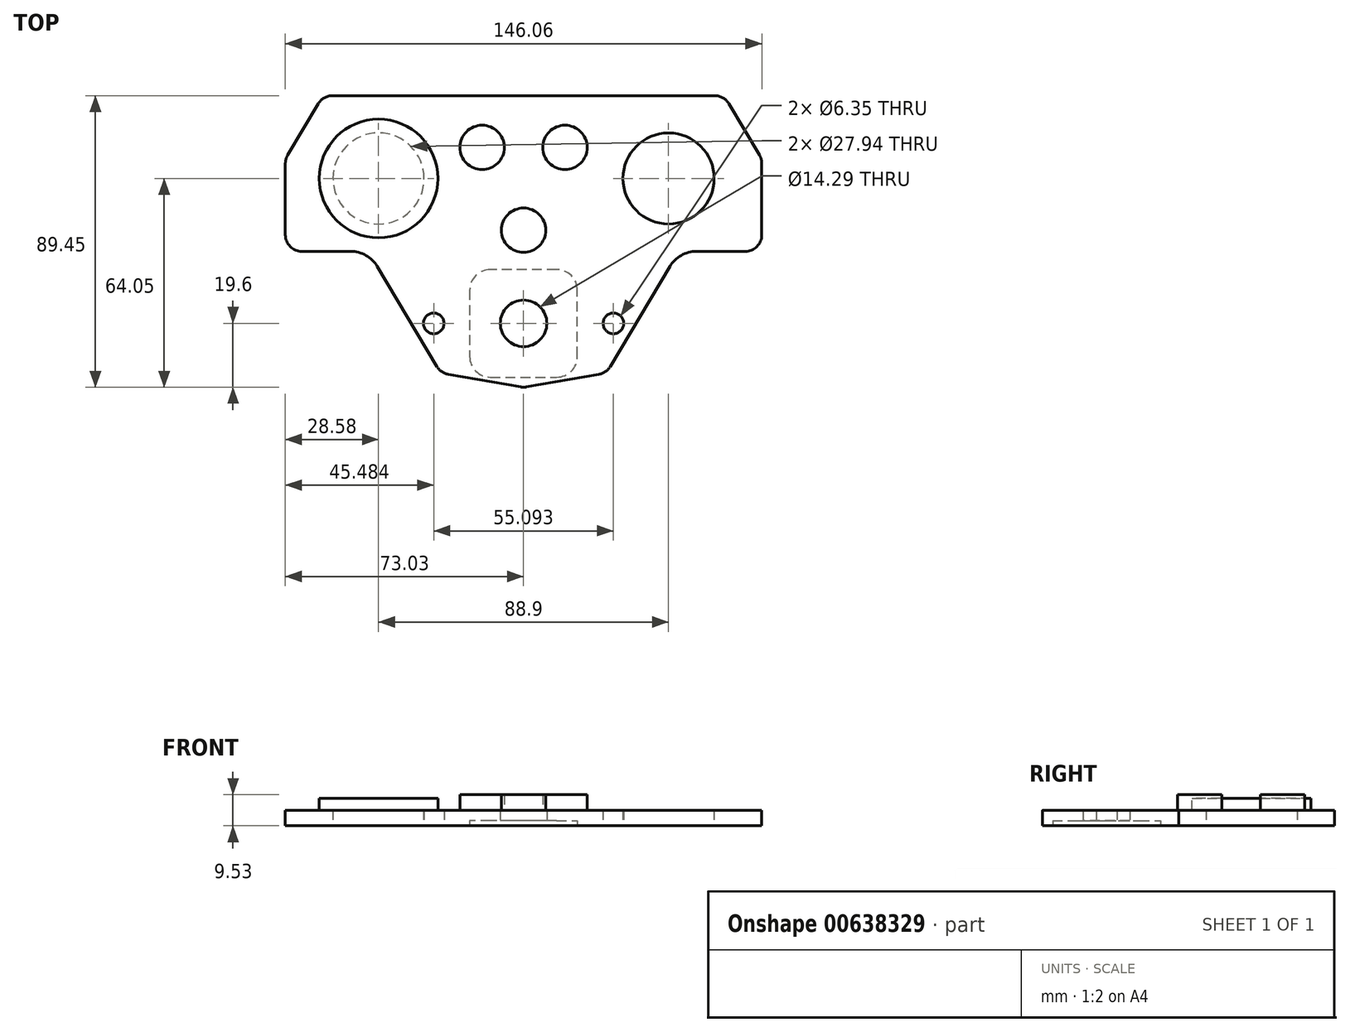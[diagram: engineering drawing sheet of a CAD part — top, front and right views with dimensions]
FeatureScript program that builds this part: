
annotation { "Feature Type Name" : "Feature", "Feature Type Description" : "" }
export const myFeature = defineFeature(function(context is Context, id is Id, definition is map)
    precondition{}
    {
        {
            var Q0;
            Q0=qCreatedBy(makeId("Top.planeOp"),FACE);
            var sketch = newSketch(context, id + "F0", { "sketchPlane" : qUnion([Q0])});
            skCircle(sketch, "E0", {"center": v(0, 0) * mm, "radius": 7.14 * mm});
            skCircle(sketch, "E1", {"center": v(27.55, 0) * mm, "radius": 3.18 * mm});
            skCircle(sketch, "E2", {"center": v(-27.55, 0) * mm, "radius": 3.18 * mm});
            skLineSegment(sketch, "E3", {"start": v(0, 29.39) * mm, "end": v(0, -33.87) * mm, "construction": true});
            skLineSegment(sketch, "E4", {"start": v(-25.4, -15.2) * mm, "end": v(0, -19.68) * mm});
            skLineSegment(sketch, "E5", {"start": v(0, -19.68) * mm, "end": v(25.4, -15.2) * mm});
            skLineSegment(sketch, "E6", {"start": v(-25.4, -15.2) * mm, "end": v(-47.63, 22.1) * mm});
            skLineSegment(sketch, "E7", {"start": v(25.4, -15.2) * mm, "end": v(47.63, 22.1) * mm});
            skLineSegment(sketch, "E8", {"start": v(47.63, 22.1) * mm, "end": v(73.03, 22.1) * mm});
            skLineSegment(sketch, "E9", {"start": v(73.03, 22.1) * mm, "end": v(73.03, 50.43) * mm});
            skLineSegment(sketch, "E10", {"start": v(73.03, 50.43) * mm, "end": v(61.45, 69.85) * mm});
            skLineSegment(sketch, "E11", {"start": v(61.45, 69.85) * mm, "end": v(0, 69.85) * mm});
            skLineSegment(sketch, "E12.MirrorCS", {"start": v(-61.45, 69.85) * mm, "end": v(0, 69.85) * mm});
            skLineSegment(sketch, "E13.MirrorCS", {"start": v(-73.03, 50.43) * mm, "end": v(-61.45, 69.85) * mm});
            skLineSegment(sketch, "E14.MirrorCS", {"start": v(-73.03, 22.1) * mm, "end": v(-73.03, 50.43) * mm});
            skLineSegment(sketch, "E15.MirrorCS", {"start": v(-47.63, 22.1) * mm, "end": v(-73.03, 22.1) * mm});
            skCircle(sketch, "E16", {"center": v(-51.23, 15.75) * mm, "radius": 6.35 * mm, "construction": true});
            skCircle(sketch, "E17", {"center": v(51.23, 15.75) * mm, "radius": 6.35 * mm, "construction": true});
            skSolve(sketch);
        }
        {
            var Q0;
            Q0=makeQuery(id+"F0.imprint","IMPRINT",FACE,{"disambiguationData":[TD([[makeQuery(id+"F0.imprint","IMPRINT",EDGE,{"derivedFrom":sQuery(id+"F0.wireOp",EDGE,"E0")}),-1.0]])]});
            extrude(context, id + "F1", {"entities" : qUnion([Q0]), "depth" : 4.76 * mm, "offsetDistance" : 25.4 * mm});
        }
        {
            var Q0;
            Q0=makeQuery(id+"F1.opExtrude","SWEPT_EDGE",EDGE,{"disambiguationData":[OSD([sQuery(id+"F0.wireOp",EDGE,"E6"),sQuery(id+"F0.wireOp",EDGE,"E15.MirrorCS")])]});
            var Q1;
            Q1=makeQuery(id+"F1.opExtrude","SWEPT_EDGE",EDGE,{"disambiguationData":[OSD([sQuery(id+"F0.wireOp",EDGE,"E7"),sQuery(id+"F0.wireOp",EDGE,"E8")])]});
            fillet(context, id + "F2", {"entities" : qUnion([Q0, Q1]), "radius" : 9.52 * mm, "tangentPropagation" : true, "allowEdgeOverflow" : false});
        }
        {
            var Q0;
            Q0=makeQuery(id+"F1.opExtrude","SWEPT_EDGE",EDGE,{"disambiguationData":[OSD([sQuery(id+"F0.wireOp",EDGE,"E14.MirrorCS"),sQuery(id+"F0.wireOp",EDGE,"E15.MirrorCS")])]});
            var Q1;
            Q1=makeQuery(id+"F1.opExtrude","SWEPT_EDGE",EDGE,{"disambiguationData":[OSD([sQuery(id+"F0.wireOp",EDGE,"E4"),sQuery(id+"F0.wireOp",EDGE,"E6")])]});
            var Q2;
            Q2=makeQuery(id+"F1.opExtrude","SWEPT_EDGE",EDGE,{"disambiguationData":[OSD([sQuery(id+"F0.wireOp",EDGE,"E4"),sQuery(id+"F0.wireOp",EDGE,"E5")])]});
            var Q3;
            Q3=makeQuery(id+"F1.opExtrude","SWEPT_EDGE",EDGE,{"disambiguationData":[OSD([sQuery(id+"F0.wireOp",EDGE,"E5"),sQuery(id+"F0.wireOp",EDGE,"E7")])]});
            var Q4;
            Q4=makeQuery(id+"F1.opExtrude","SWEPT_EDGE",EDGE,{"disambiguationData":[OSD([sQuery(id+"F0.wireOp",EDGE,"E8"),sQuery(id+"F0.wireOp",EDGE,"E9")])]});
            var Q5;
            Q5=makeQuery(id+"F1.opExtrude","SWEPT_EDGE",EDGE,{"disambiguationData":[OSD([sQuery(id+"F0.wireOp",EDGE,"E9"),sQuery(id+"F0.wireOp",EDGE,"E10")])]});
            var Q6;
            Q6=makeQuery(id+"F1.opExtrude","SWEPT_EDGE",EDGE,{"disambiguationData":[OSD([sQuery(id+"F0.wireOp",EDGE,"E10"),sQuery(id+"F0.wireOp",EDGE,"E11")])]});
            var Q7;
            Q7=makeQuery(id+"F1.opExtrude","SWEPT_EDGE",EDGE,{"disambiguationData":[OSD([sQuery(id+"F0.wireOp",EDGE,"E13.MirrorCS"),sQuery(id+"F0.wireOp",EDGE,"E14.MirrorCS")])]});
            var Q8;
            Q8=makeQuery(id+"F1.opExtrude","SWEPT_EDGE",EDGE,{"disambiguationData":[OSD([sQuery(id+"F0.wireOp",EDGE,"E12.MirrorCS"),sQuery(id+"F0.wireOp",EDGE,"E13.MirrorCS")])]});
            fillet(context, id + "F3", {"entities" : qUnion([Q0, Q1, Q2, Q3, Q4, Q5, Q6, Q7, Q8]), "radius" : 5.08 * mm, "tangentPropagation" : true, "allowEdgeOverflow" : false});
        }
        {
            var Q0;
            Q0=qCreatedBy(makeId("Top.planeOp"),FACE);
            var sketch = newSketch(context, id + "F4", { "sketchPlane" : qUnion([Q0])});
            skCircle(sketch, "E18", {"center": v(-44.45, 44.45) * mm, "radius": 13.97 * mm});
            skLineSegment(sketch, "E19", {"start": v(0, 0) * mm, "end": v(0, 69.85) * mm, "construction": true});
            skCircle(sketch, "E20.MirrorC", {"center": v(44.45, 44.45) * mm, "radius": 13.97 * mm});
            skSolve(sketch);
        }
        {
            var Q0;
            Q0 = qSketchRegion(id + "F4", true);
            extrude(context, id + "F5", {"entities" : qUnion([Q0]), "operationType" : NewBodyOperationType.REMOVE, "depth" : 25.4 * mm, "offsetDistance" : 25.4 * mm});
        }
        {
            var Q0;
            Q0=qCreatedBy(makeId("Top.planeOp"),FACE);
            var sketch = newSketch(context, id + "F6", { "sketchPlane" : qUnion([Q0])});
            skArc(sketch, "E21", {"start": v(-16.51, -10.16) * mm, "mid": v(-14.65, -14.65) * mm, "end": v(-10.16, -16.51) * mm});
            skArc(sketch, "E22", {"start": v(-10.16, 16.51) * mm, "mid": v(-14.65, 14.65) * mm, "end": v(-16.51, 10.16) * mm});
            skLineSegment(sketch, "E23", {"start": v(-23.42, 0) * mm, "end": v(23.42, 0) * mm, "construction": true});
            skLineSegment(sketch, "E24", {"start": v(0, -20.58) * mm, "end": v(0, 20.58) * mm, "construction": true});
            skArc(sketch, "E25.MirrorC", {"start": v(10.16, 16.51) * mm, "mid": v(14.65, 14.65) * mm, "end": v(16.51, 10.16) * mm});
            skArc(sketch, "E26.MirrorC", {"start": v(16.51, -10.16) * mm, "mid": v(14.65, -14.65) * mm, "end": v(10.16, -16.51) * mm});
            skLineSegment(sketch, "E27", {"start": v(-10.16, -16.51) * mm, "end": v(10.16, -16.51) * mm});
            skLineSegment(sketch, "E28", {"start": v(16.51, -10.16) * mm, "end": v(16.51, 10.16) * mm});
            skLineSegment(sketch, "E29", {"start": v(10.16, 16.51) * mm, "end": v(-10.16, 16.51) * mm});
            skLineSegment(sketch, "E30", {"start": v(-16.51, 10.16) * mm, "end": v(-16.51, -10.16) * mm});
            skSolve(sketch);
        }
        {
            var Q0;
            Q0=makeQuery(id+"F6.imprint","IMPRINT",FACE,{"disambiguationData":[TD([[makeQuery(id+"F6.imprint","IMPRINT",EDGE,{"derivedFrom":sQuery(id+"F6.wireOp",EDGE,"E21")}),1.0]])]});
            extrude(context, id + "F7", {"entities" : qUnion([Q0]), "operationType" : NewBodyOperationType.REMOVE, "depth" : 1.52 * mm, "offsetDistance" : 25.4 * mm});
        }
        {
            var Q0;
            Q0=qCreatedBy(makeId("Front.planeOp"),FACE);
            cPlane(context, id + "F8", {"entities" : qUnion([Q0]), "cplaneType" : CPlaneType.OFFSET, "offset" : 44.45 * mm, "oppositeDirection" : true, "width" : 152.4 * mm, "height" : 152.4 * mm});
        }
        {
            var Q0;
            Q0=qCreatedBy(makeId("Right.planeOp"),FACE);
            cPlane(context, id + "F9", {"entities" : qUnion([Q0]), "cplaneType" : CPlaneType.OFFSET, "offset" : 44.45 * mm, "oppositeDirection" : true, "width" : 152.4 * mm, "height" : 152.4 * mm});
        }
        {
            var Q0;
            Q0=qCreatedBy(id+"F8.planeOp",FACE);
            var sketch = newSketch(context, id + "F10", { "sketchPlane" : qUnion([Q0])});
            skLineSegment(sketch, "E31", {"start": v(-44.45, 30.16) * mm, "end": v(-44.45, -35.09) * mm, "construction": true});
            skLineSegment(sketch, "E32.bottom", {"start": v(-44.45, 8.4) * mm, "end": v(-26.26, 8.4) * mm});
            skLineSegment(sketch, "E32.top", {"start": v(-44.45, 4.76) * mm, "end": v(-26.26, 4.76) * mm});
            skLineSegment(sketch, "E32.left", {"start": v(-44.45, 8.4) * mm, "end": v(-44.45, 4.76) * mm});
            skLineSegment(sketch, "E32.right", {"start": v(-26.26, 8.4) * mm, "end": v(-26.26, 4.76) * mm});
            skSolve(sketch);
        }
        {
            var Q0;
            Q0 = qSketchRegion(id + "F10", true);
            var Q1;
            Q1=sQuery(id+"F10.wireOp",EDGE,"E31");
            revolve(context, id + "F11", {"entities" : qUnion([Q0]), "axis" : qUnion([Q1]), "revolveType" : RevolveType.FULL});
        }
        {
            var Q0;
            Q0=makeQuery(id+"F1.opExtrude","CAP_FACE",FACE,{"disambiguationData":[OSD([sQuery(id+"F0.wireOp",EDGE,"E0"),sQuery(id+"F0.wireOp",EDGE,"E1"),sQuery(id+"F0.wireOp",EDGE,"E2"),sQuery(id+"F0.wireOp",EDGE,"E4"),sQuery(id+"F0.wireOp",EDGE,"E5"),sQuery(id+"F0.wireOp",EDGE,"E6"),sQuery(id+"F0.wireOp",EDGE,"E7"),sQuery(id+"F0.wireOp",EDGE,"E8"),sQuery(id+"F0.wireOp",EDGE,"E9"),sQuery(id+"F0.wireOp",EDGE,"E10"),sQuery(id+"F0.wireOp",EDGE,"E11"),sQuery(id+"F0.wireOp",EDGE,"E12.MirrorCS"),sQuery(id+"F0.wireOp",EDGE,"E13.MirrorCS"),sQuery(id+"F0.wireOp",EDGE,"E14.MirrorCS"),sQuery(id+"F0.wireOp",EDGE,"E15.MirrorCS")])],"isStart":false});
            var sketch = newSketch(context, id + "F12", { "sketchPlane" : qUnion([Q0])});
            skCircle(sketch, "E33", {"center": v(-12.7, 53.98) * mm, "radius": 6.8 * mm});
            skCircle(sketch, "E34", {"center": v(0, 28.58) * mm, "radius": 6.8 * mm});
            skCircle(sketch, "E35.MirrorC", {"center": v(12.7, 53.98) * mm, "radius": 6.8 * mm});
            skSolve(sketch);
        }
        {
            var Q0;
            Q0 = qSketchRegion(id + "F12", true);
            extrude(context, id + "F13", {"entities" : qUnion([Q0]), "depth" : 4.76 * mm, "offsetDistance" : 25.4 * mm});
        }
    });
